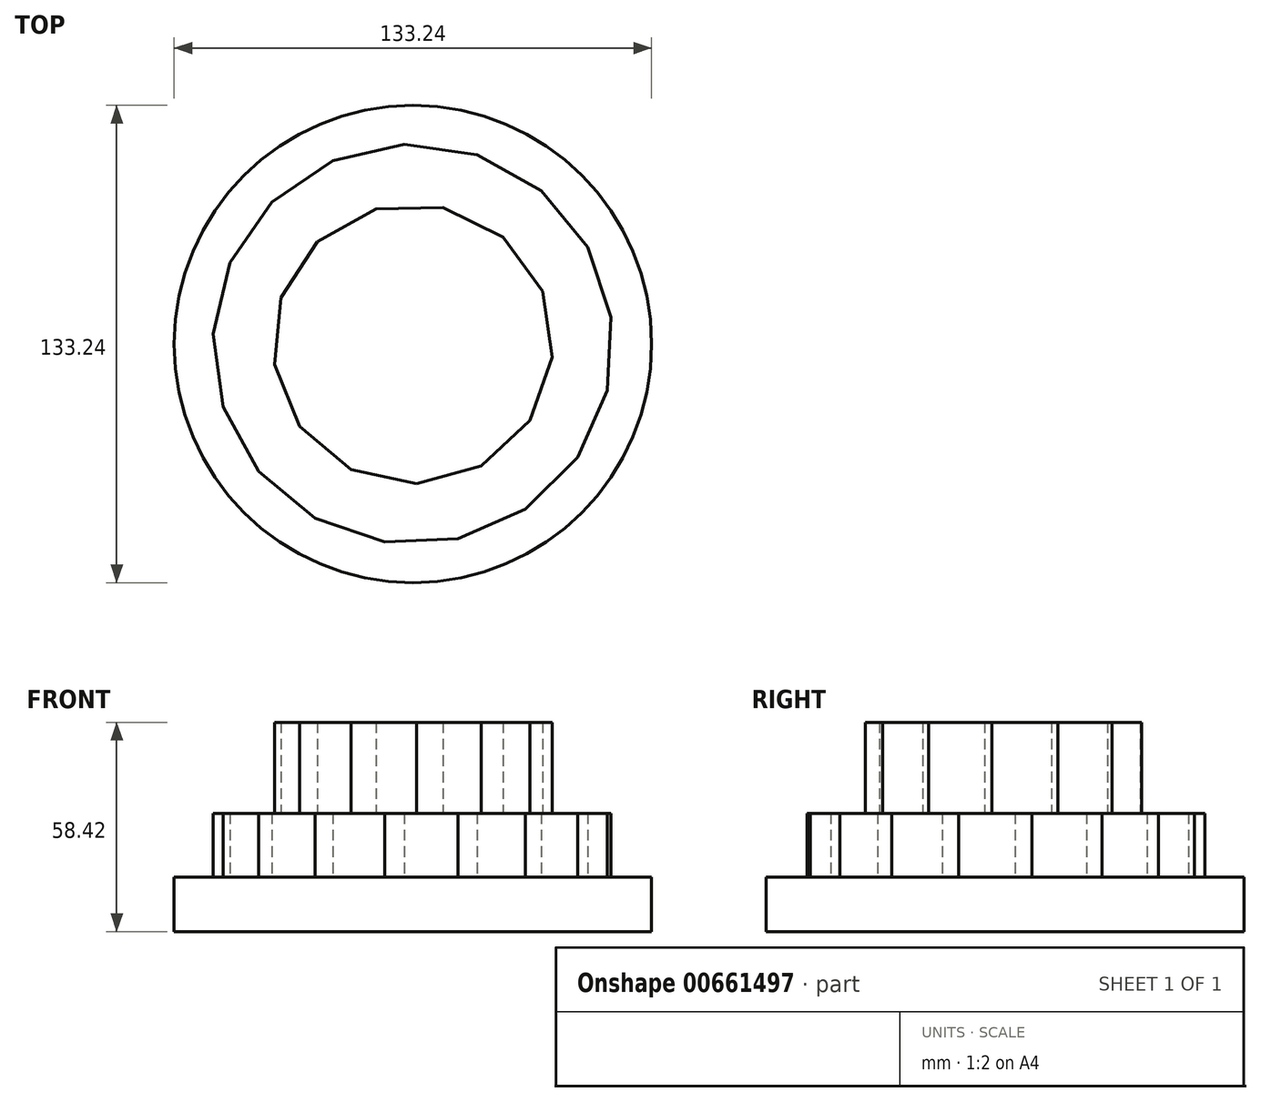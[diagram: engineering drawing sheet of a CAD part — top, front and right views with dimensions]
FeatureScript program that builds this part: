
annotation { "Feature Type Name" : "Feature", "Feature Type Description" : "" }
export const myFeature = defineFeature(function(context is Context, id is Id, definition is map)
    precondition{}
    {
        {
            var Q0;
            Q0=qCreatedBy(makeId("Top.planeOp"),FACE);
            var sketch = newSketch(context, id + "F0", { "sketchPlane" : qUnion([Q0])});
            skCircle(sketch, "E0", {"center": v(0, 0) * mm, "radius": 66.62 * mm});
            skSolve(sketch);
        }
        {
            var Q0;
            Q0=makeQuery(id+"F0.imprint","IMPRINT",FACE,{"disambiguationData":[TD([[makeQuery(id+"F0.imprint","IMPRINT",EDGE,{"derivedFrom":sQuery(id+"F0.wireOp",EDGE,"E0")}),1.0]])]});
            extrude(context, id + "F1", {"entities" : qUnion([Q0]), "depth" : 15.24 * mm, "offsetDistance" : 25.4 * mm});
        }
        {
            var Q0;
            Q0=makeQuery(id+"F1.opExtrude","CAP_FACE",FACE,{"disambiguationData":[OSD([sQuery(id+"F0.wireOp",EDGE,"E0")])],"isStart":false});
            var sketch = newSketch(context, id + "F2", { "sketchPlane" : qUnion([Q0])});
            skCircle(sketch, "E1.cCircle", {"center": v(0, 0) * mm, "radius": 54.85 * mm, "construction": true});
            skLineSegment(sketch, "E1.0", {"start": v(-50.98, 22.7) * mm, "end": v(-39.33, 39.59) * mm});
            skLineSegment(sketch, "E1.1", {"start": v(-39.33, 39.59) * mm, "end": v(-22.37, 51.12) * mm});
            skLineSegment(sketch, "E1.2", {"start": v(-22.37, 51.12) * mm, "end": v(-2.4, 55.75) * mm});
            skLineSegment(sketch, "E1.3", {"start": v(-2.4, 55.75) * mm, "end": v(17.9, 52.85) * mm});
            skLineSegment(sketch, "E1.4", {"start": v(17.9, 52.85) * mm, "end": v(35.8, 42.82) * mm});
            skLineSegment(sketch, "E1.5", {"start": v(35.8, 42.82) * mm, "end": v(48.84, 27) * mm});
            skLineSegment(sketch, "E1.6", {"start": v(48.84, 27) * mm, "end": v(55.3, 7.53) * mm});
            skLineSegment(sketch, "E1.7", {"start": v(55.3, 7.53) * mm, "end": v(54.28, -12.95) * mm});
            skLineSegment(sketch, "E1.8", {"start": v(54.28, -12.95) * mm, "end": v(45.93, -31.69) * mm});
            skLineSegment(sketch, "E1.9", {"start": v(45.93, -31.69) * mm, "end": v(31.39, -46.14) * mm});
            skLineSegment(sketch, "E1.10", {"start": v(31.39, -46.14) * mm, "end": v(12.6, -54.36) * mm});
            skLineSegment(sketch, "E1.11", {"start": v(12.6, -54.36) * mm, "end": v(-7.9, -55.24) * mm});
            skLineSegment(sketch, "E1.12", {"start": v(-7.9, -55.24) * mm, "end": v(-27.31, -48.66) * mm});
            skLineSegment(sketch, "E1.13", {"start": v(-27.31, -48.66) * mm, "end": v(-43.05, -35.5) * mm});
            skLineSegment(sketch, "E1.14", {"start": v(-43.05, -35.5) * mm, "end": v(-52.97, -17.56) * mm});
            skLineSegment(sketch, "E1.15", {"start": v(-52.97, -17.56) * mm, "end": v(-55.74, 2.76) * mm});
            skLineSegment(sketch, "E1.16", {"start": v(-55.74, 2.76) * mm, "end": v(-50.98, 22.7) * mm});
            skPoint(sketch, "E1.0.midPoint", {"position": v(-45.15, 31.15) * mm});
            skSolve(sketch);
        }
        {
            var Q0;
            Q0 = qSketchRegion(id + "F2", true);
            extrude(context, id + "F3", {"entities" : qUnion([Q0]), "operationType" : NewBodyOperationType.ADD, "depth" : 17.78 * mm, "offsetDistance" : 25.4 * mm});
        }
        {
            var Q0;
            Q0=makeQuery(id+"F3.opExtrude","CAP_FACE",FACE,{"disambiguationData":[OSD([sQuery(id+"F2.wireOp",EDGE,"E1.0"),sQuery(id+"F2.wireOp",EDGE,"E1.1"),sQuery(id+"F2.wireOp",EDGE,"E1.2"),sQuery(id+"F2.wireOp",EDGE,"E1.3"),sQuery(id+"F2.wireOp",EDGE,"E1.4"),sQuery(id+"F2.wireOp",EDGE,"E1.5"),sQuery(id+"F2.wireOp",EDGE,"E1.6"),sQuery(id+"F2.wireOp",EDGE,"E1.7"),sQuery(id+"F2.wireOp",EDGE,"E1.8"),sQuery(id+"F2.wireOp",EDGE,"E1.9"),sQuery(id+"F2.wireOp",EDGE,"E1.10"),sQuery(id+"F2.wireOp",EDGE,"E1.11"),sQuery(id+"F2.wireOp",EDGE,"E1.12"),sQuery(id+"F2.wireOp",EDGE,"E1.13"),sQuery(id+"F2.wireOp",EDGE,"E1.14"),sQuery(id+"F2.wireOp",EDGE,"E1.15"),sQuery(id+"F2.wireOp",EDGE,"E1.16")])],"isStart":false});
            var sketch = newSketch(context, id + "F4", { "sketchPlane" : qUnion([Q0])});
            skCircle(sketch, "E2.cCircle", {"center": v(0, 0) * mm, "radius": 37.92 * mm, "construction": true});
            skLineSegment(sketch, "E2.0", {"start": v(-17.25, -35.03) * mm, "end": v(-31.56, -23) * mm});
            skLineSegment(sketch, "E2.1", {"start": v(-31.56, -23) * mm, "end": v(-38.63, -5.7) * mm});
            skLineSegment(sketch, "E2.2", {"start": v(-38.63, -5.7) * mm, "end": v(-36.86, 12.9) * mm});
            skLineSegment(sketch, "E2.3", {"start": v(-36.86, 12.9) * mm, "end": v(-26.64, 28.55) * mm});
            skLineSegment(sketch, "E2.4", {"start": v(-26.64, 28.55) * mm, "end": v(-10.32, 37.66) * mm});
            skLineSegment(sketch, "E2.5", {"start": v(-10.32, 37.66) * mm, "end": v(8.37, 38.14) * mm});
            skLineSegment(sketch, "E2.6", {"start": v(8.37, 38.14) * mm, "end": v(25.13, 29.89) * mm});
            skLineSegment(sketch, "E2.7", {"start": v(25.13, 29.89) * mm, "end": v(36.14, 14.78) * mm});
            skLineSegment(sketch, "E2.8", {"start": v(36.14, 14.78) * mm, "end": v(38.87, -3.7) * mm});
            skLineSegment(sketch, "E2.9", {"start": v(38.87, -3.7) * mm, "end": v(32.7, -21.35) * mm});
            skLineSegment(sketch, "E2.10", {"start": v(32.7, -21.35) * mm, "end": v(19.03, -34.1) * mm});
            skLineSegment(sketch, "E2.11", {"start": v(19.03, -34.1) * mm, "end": v(1, -39.04) * mm});
            skLineSegment(sketch, "E2.12", {"start": v(1, -39.04) * mm, "end": v(-17.25, -35.03) * mm});
            skPoint(sketch, "E2.0.midPoint", {"position": v(-24.4, -29.02) * mm});
            skSolve(sketch);
        }
        {
            var Q0;
            Q0 = qSketchRegion(id + "F4", true);
            extrude(context, id + "F5", {"entities" : qUnion([Q0]), "operationType" : NewBodyOperationType.ADD, "depth" : 25.4 * mm, "offsetDistance" : 25.4 * mm});
        }
    });
